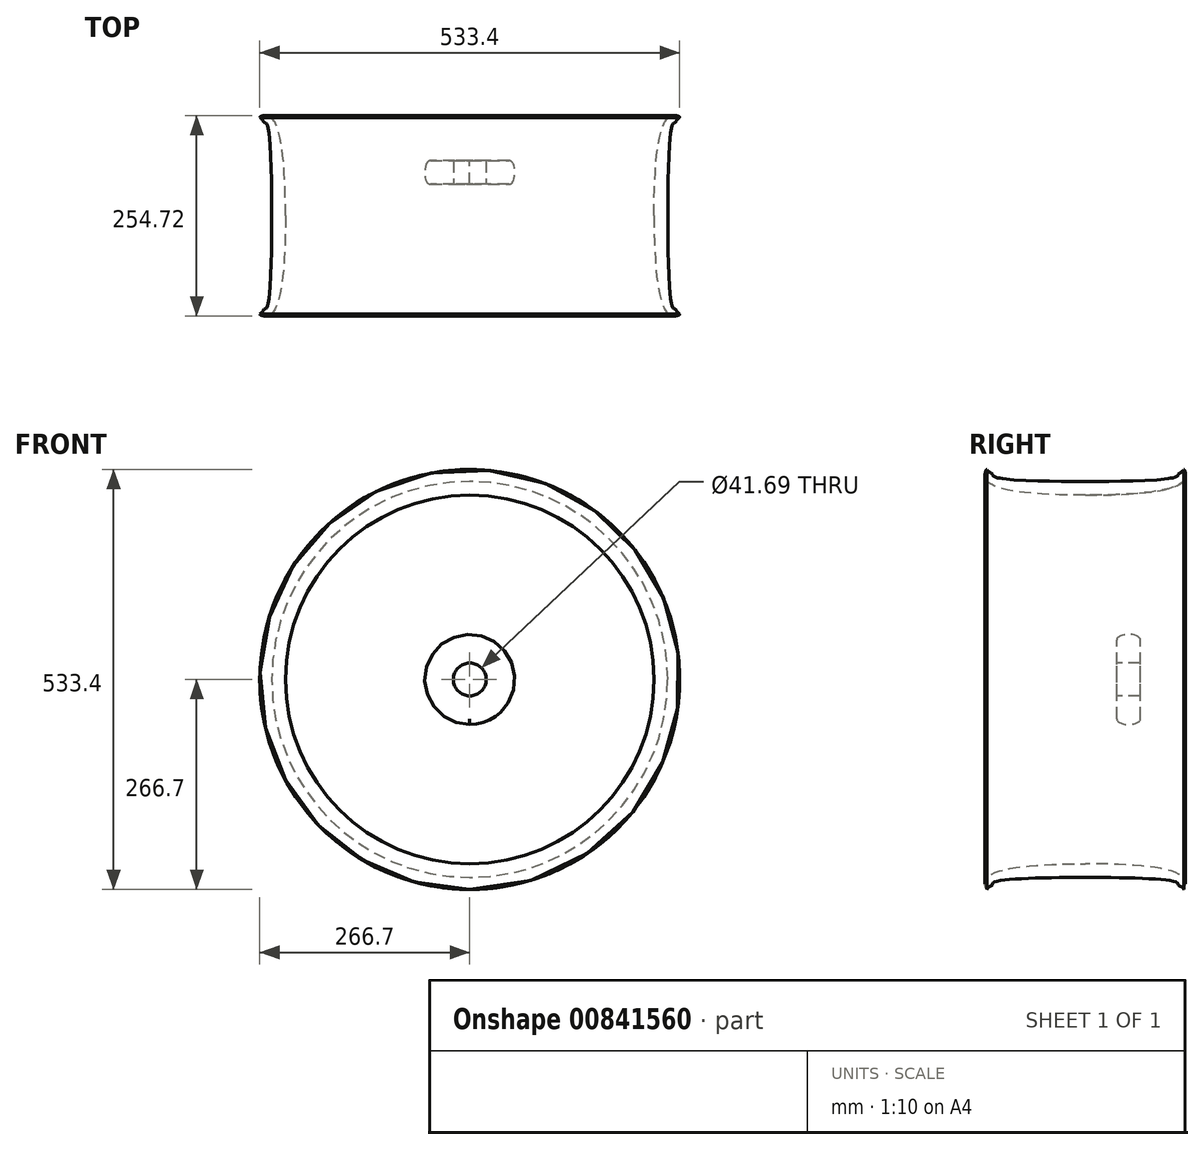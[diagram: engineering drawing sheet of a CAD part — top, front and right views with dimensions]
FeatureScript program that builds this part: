
annotation { "Feature Type Name" : "Feature", "Feature Type Description" : "" }
export const myFeature = defineFeature(function(context is Context, id is Id, definition is map)
    precondition{}
    {
        {
            var Q0;
            Q0=qCreatedBy(makeId("Right.planeOp"),FACE);
            var sketch = newSketch(context, id + "F0", { "sketchPlane" : qUnion([Q0])});
            skPoint(sketch, "E0", {"position": v(0, 266.7) * mm});
            skLineSegment(sketch, "E1", {"start": v(-125, 266.7) * mm, "end": v(125, 266.7) * mm, "construction": true});
            skFitSpline(sketch, "E2", {"points": [v(-125, 266.7) * mm, v(-120.5, 262.5) * mm, v(-118.33, 260.98) * mm, v(-117.16, 258.44) * mm, v(0, 251.5) * mm], "startDerivative": vector(22.5, -44.9) * mm, "endDerivative": vector(251.68, 0) * mm});
            skLineSegment(sketch, "E3", {"start": v(0, 487.06) * mm, "end": v(0, 266.7) * mm, "construction": true});
            skFitSpline(sketch, "E4", {"points": [v(-125, 266.7) * mm, v(-126, 265.92) * mm, v(-125.63, 253.22) * mm, v(0, 234.12) * mm], "startDerivative": vector(-21.47, 0.55) * mm, "endDerivative": vector(246.96, 0) * mm});
            skFitSpline(sketch, "E5.MirrorCS", {"points": [v(125, 266.7) * mm, v(120.5, 262.5) * mm, v(118.33, 260.98) * mm, v(117.16, 258.44) * mm, v(0, 251.5) * mm], "startDerivative": vector(-22.5, -44.9) * mm, "endDerivative": vector(-251.68, 0) * mm});
            skFitSpline(sketch, "E6.MirrorCS", {"points": [v(125, 266.7) * mm, v(126, 265.92) * mm, v(125.63, 253.22) * mm, v(0, 234.12) * mm], "startDerivative": vector(21.47, 0.55) * mm, "endDerivative": vector(-246.96, 0) * mm});
            skLineSegment(sketch, "E7", {"start": v(-17.91, 0) * mm, "end": v(66.6, 0) * mm, "construction": true});
            skLineSegment(sketch, "E8", {"start": v(70, 0) * mm, "end": v(70, 50) * mm});
            skLineSegment(sketch, "E9", {"start": v(40, 0) * mm, "end": v(40, 50) * mm});
            skFitSpline(sketch, "E10", {"points": [v(40, 50) * mm, v(70, 50) * mm], "startDerivative": vector(0, 28.8) * mm, "endDerivative": vector(0, -28.6) * mm});
            skLineSegment(sketch, "E11", {"start": v(40, 0) * mm, "end": v(70, 0) * mm});
            skSolve(sketch);
        }
        {
            var Q0;
            Q0=qSketchRegion(id+"F0",true);
            var Q1;
            Q1=sQuery(id+"F0.wireOp",EDGE,"E7");
            revolve(context, id + "F1", {"surfaceOperationType" : NewSurfaceOperationType.NEW, "entities" : qUnion([Q0]), "axis" : qUnion([Q1]), "revolveType" : RevolveType.FULL});
        }
        {
            var Q0;
            Q0=makeQuery(id+"F1.opRevolve","SWEPT_FACE",FACE,{"disambiguationData":[OSD([sQuery(id+"F0.wireOp",EDGE,"E9")])]});
            var sketch = newSketch(context, id + "F2", { "sketchPlane" : qUnion([Q0])});
            skCircle(sketch, "E12", {"center": v(0, 0) * mm, "radius": 20.84 * mm});
            skSolve(sketch);
        }
        {
            var Q0;
            Q0=makeQuery(id+"F2.imprint","IMPRINT",FACE,{"disambiguationData":[TD([[makeQuery(id+"F2.imprint","IMPRINT",EDGE,{"derivedFrom":sQuery(id+"F2.wireOp",EDGE,"E12")}),1.0]])]});
            extrude(context, id + "F3", {"entities" : qUnion([Q0]), "operationType" : NewBodyOperationType.REMOVE, "oppositeDirection" : true, "depth" : 25 * mm, "offsetDistance" : 25 * mm});
        }
        {
            var Q0;
            Q0=makeQuery(id+"F3.boolean.opBoolean","COPY",FACE,{"derivedFrom":makeQuery(id+"F3.opExtrude","CAP_FACE",FACE,{"disambiguationData":[OSD([sQuery(id+"F2.wireOp",EDGE,"E12")])],"isStart":false})});
            extrude(context, id + "F4", {"entities" : qUnion([Q0]), "operationType" : NewBodyOperationType.REMOVE, "oppositeDirection" : true, "depth" : 50 * mm, "offsetDistance" : 25 * mm});
        }
    });
